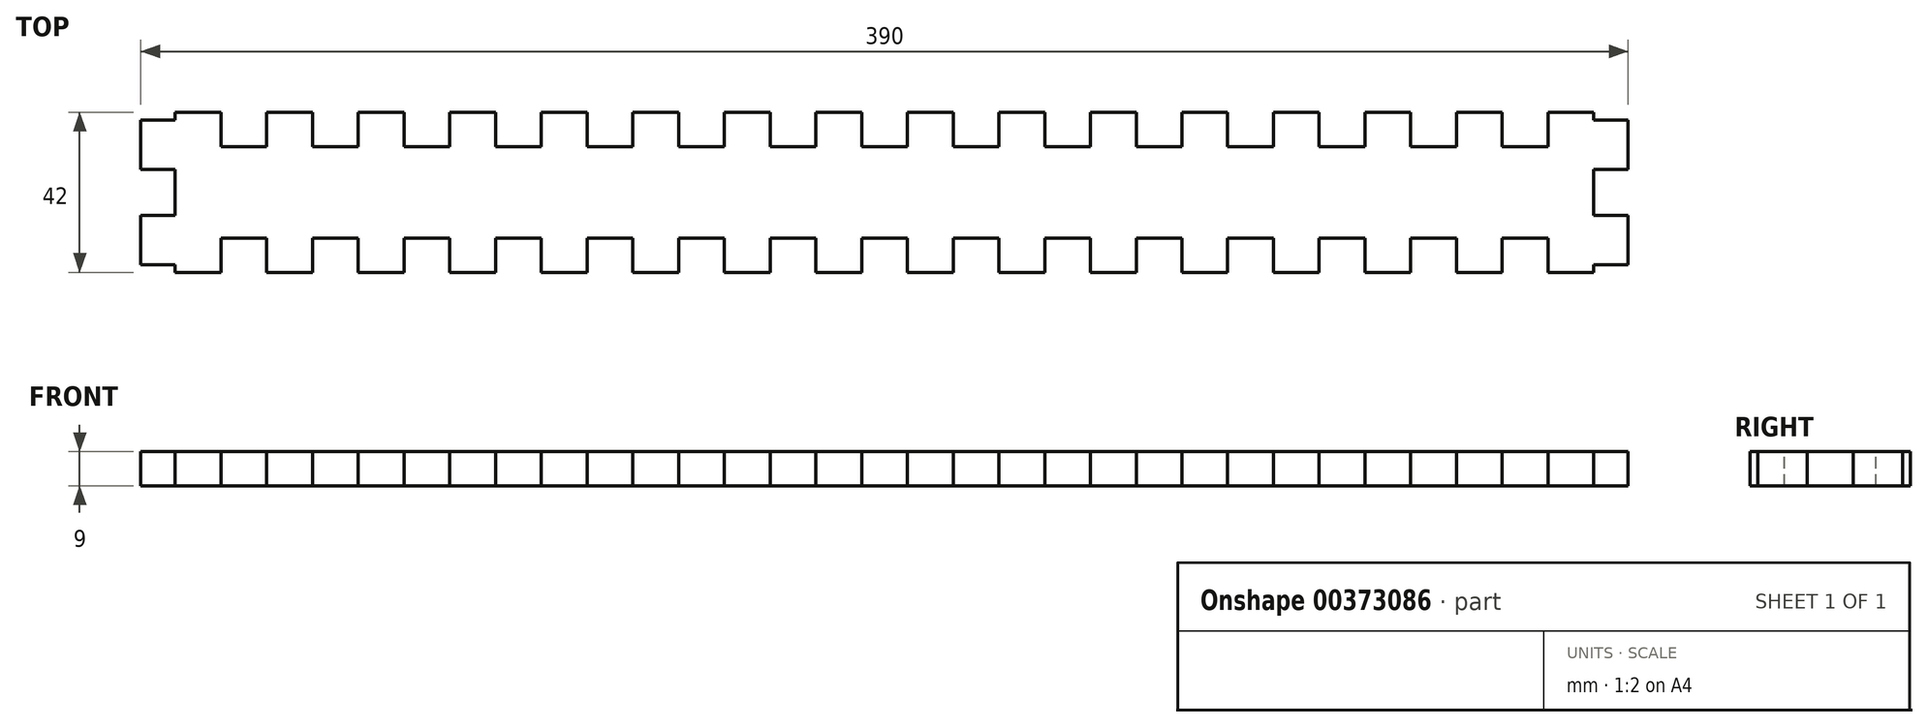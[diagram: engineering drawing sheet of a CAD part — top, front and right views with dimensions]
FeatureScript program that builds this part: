
annotation { "Feature Type Name" : "Feature", "Feature Type Description" : "" }
export const myFeature = defineFeature(function(context is Context, id is Id, definition is map)
    precondition{}
    {
        {
            var Q0;
            Q0=qCreatedBy(makeId("Top.planeOp"),FACE);
            var sketch = newSketch(context, id + "F0", { "sketchPlane" : qUnion([Q0])});
            skLineSegment(sketch, "E0.bottom", {"start": v(-198, 12) * mm, "end": v(198, 12) * mm});
            skLineSegment(sketch, "E0.top", {"start": v(-198, -12) * mm, "end": v(198, -12) * mm});
            skLineSegment(sketch, "E0.left", {"start": v(-198, 12) * mm, "end": v(-198, -12) * mm});
            skLineSegment(sketch, "E0.right", {"start": v(198, 12) * mm, "end": v(198, -12) * mm});
            skPoint(sketch, "E0.middle", {"position": v(0, 0) * mm});
            skSolve(sketch);
        }
        {
            var Q0;
            Q0 = qSketchRegion(id + "F0", true);
            extrude(context, id + "F1", {"entities" : qUnion([Q0]), "depth" : 9 * mm});
        }
        {
            var Q0;
            Q0=makeQuery(id+"F1.opExtrude","CAP_FACE",FACE,{"disambiguationData":[OSD([sQuery(id+"F0.wireOp",EDGE,"E0.bottom"),sQuery(id+"F0.wireOp",EDGE,"E0.top"),sQuery(id+"F0.wireOp",EDGE,"E0.left"),sQuery(id+"F0.wireOp",EDGE,"E0.right")])],"isStart":false});
            var sketch = newSketch(context, id + "F2", { "sketchPlane" : qUnion([Q0])});
            skLineSegment(sketch, "E1", {"start": v(0, 0) * mm, "end": v(0, -12) * mm, "construction": true});
            skLineSegment(sketch, "E2", {"start": v(0, -12) * mm, "end": v(6, -12) * mm, "construction": true});
            skLineSegment(sketch, "E3.bottom", {"start": v(6, -12) * mm, "end": v(18, -12) * mm});
            skLineSegment(sketch, "E3.top", {"start": v(6, -21) * mm, "end": v(18, -21) * mm});
            skLineSegment(sketch, "E3.left", {"start": v(6, -12) * mm, "end": v(6, -21) * mm});
            skLineSegment(sketch, "E3.right", {"start": v(18, -12) * mm, "end": v(18, -21) * mm});
            skLineSegment(sketch, "E4.direction1", {"start": v(6, -21) * mm, "end": v(18, -21) * mm, "construction": true});
            skLineSegment(sketch, "E5.1.0.0", {"start": v(30, -12) * mm, "end": v(30, -21) * mm});
            skLineSegment(sketch, "E5.1.0.1", {"start": v(30, -12) * mm, "end": v(42, -12) * mm});
            skLineSegment(sketch, "E5.1.0.2", {"start": v(42, -12) * mm, "end": v(42, -21) * mm});
            skLineSegment(sketch, "E5.1.0.3", {"start": v(30, -21) * mm, "end": v(42, -21) * mm});
            skLineSegment(sketch, "E5.2.0.0", {"start": v(54, -12) * mm, "end": v(54, -21) * mm});
            skLineSegment(sketch, "E5.2.0.1", {"start": v(54, -12) * mm, "end": v(66, -12) * mm});
            skLineSegment(sketch, "E5.2.0.2", {"start": v(66, -12) * mm, "end": v(66, -21) * mm});
            skLineSegment(sketch, "E5.2.0.3", {"start": v(54, -21) * mm, "end": v(66, -21) * mm});
            skLineSegment(sketch, "E5.3.0.0", {"start": v(78, -12) * mm, "end": v(78, -21) * mm});
            skLineSegment(sketch, "E5.3.0.1", {"start": v(78, -12) * mm, "end": v(90, -12) * mm});
            skLineSegment(sketch, "E5.3.0.2", {"start": v(90, -12) * mm, "end": v(90, -21) * mm});
            skLineSegment(sketch, "E5.3.0.3", {"start": v(78, -21) * mm, "end": v(90, -21) * mm});
            skLineSegment(sketch, "E5.4.0.0", {"start": v(102, -12) * mm, "end": v(102, -21) * mm});
            skLineSegment(sketch, "E5.4.0.1", {"start": v(102, -12) * mm, "end": v(114, -12) * mm});
            skLineSegment(sketch, "E5.4.0.2", {"start": v(114, -12) * mm, "end": v(114, -21) * mm});
            skLineSegment(sketch, "E5.4.0.3", {"start": v(102, -21) * mm, "end": v(114, -21) * mm});
            skLineSegment(sketch, "E5.5.0.0", {"start": v(126, -12) * mm, "end": v(126, -21) * mm});
            skLineSegment(sketch, "E5.5.0.1", {"start": v(126, -12) * mm, "end": v(138, -12) * mm});
            skLineSegment(sketch, "E5.5.0.2", {"start": v(138, -12) * mm, "end": v(138, -21) * mm});
            skLineSegment(sketch, "E5.5.0.3", {"start": v(126, -21) * mm, "end": v(138, -21) * mm});
            skLineSegment(sketch, "E5.6.0.0", {"start": v(150, -12) * mm, "end": v(150, -21) * mm});
            skLineSegment(sketch, "E5.6.0.1", {"start": v(150, -12) * mm, "end": v(162, -12) * mm});
            skLineSegment(sketch, "E5.6.0.2", {"start": v(162, -12) * mm, "end": v(162, -21) * mm});
            skLineSegment(sketch, "E5.6.0.3", {"start": v(150, -21) * mm, "end": v(162, -21) * mm});
            skLineSegment(sketch, "E5.7.0.0", {"start": v(174, -12) * mm, "end": v(174, -21) * mm});
            skLineSegment(sketch, "E5.7.0.1", {"start": v(174, -12) * mm, "end": v(186, -12) * mm});
            skLineSegment(sketch, "E5.7.0.2", {"start": v(186, -12) * mm, "end": v(186, -21) * mm});
            skLineSegment(sketch, "E5.7.0.3", {"start": v(174, -21) * mm, "end": v(186, -21) * mm});
            skLineSegment(sketch, "E5.direction1", {"start": v(6, -21) * mm, "end": v(30, -21) * mm, "construction": true});
            skLineSegment(sketch, "E6.MirrorCS", {"start": v(-6, -21) * mm, "end": v(-18, -21) * mm});
            skLineSegment(sketch, "E7.MirrorCS", {"start": v(0, -12) * mm, "end": v(-6, -12) * mm, "construction": true});
            skLineSegment(sketch, "E8.MirrorCS", {"start": v(-6, -12) * mm, "end": v(-6, -21) * mm});
            skLineSegment(sketch, "E9.MirrorCS", {"start": v(-6, -21) * mm, "end": v(-18, -21) * mm, "construction": true});
            skLineSegment(sketch, "E10.MirrorCS", {"start": v(-6, -21) * mm, "end": v(-30, -21) * mm, "construction": true});
            skLineSegment(sketch, "E11.MirrorCS", {"start": v(-66, -12) * mm, "end": v(-66, -21) * mm});
            skLineSegment(sketch, "E12.MirrorCS", {"start": v(-54, -21) * mm, "end": v(-66, -21) * mm});
            skLineSegment(sketch, "E13.MirrorCS", {"start": v(-78, -12) * mm, "end": v(-78, -21) * mm});
            skLineSegment(sketch, "E14.MirrorCS", {"start": v(-6, -12) * mm, "end": v(-18, -12) * mm});
            skLineSegment(sketch, "E15.MirrorCS", {"start": v(-126, -12) * mm, "end": v(-126, -21) * mm});
            skLineSegment(sketch, "E16.MirrorCS", {"start": v(-150, -12) * mm, "end": v(-150, -21) * mm});
            skLineSegment(sketch, "E17.MirrorCS", {"start": v(-162, -12) * mm, "end": v(-162, -21) * mm});
            skLineSegment(sketch, "E18.MirrorCS", {"start": v(-18, -12) * mm, "end": v(-18, -21) * mm});
            skLineSegment(sketch, "E19.MirrorCS", {"start": v(-30, -12) * mm, "end": v(-30, -21) * mm});
            skLineSegment(sketch, "E20.MirrorCS", {"start": v(-30, -12) * mm, "end": v(-42, -12) * mm});
            skLineSegment(sketch, "E21.MirrorCS", {"start": v(-102, -12) * mm, "end": v(-114, -12) * mm});
            skLineSegment(sketch, "E22.MirrorCS", {"start": v(-174, -12) * mm, "end": v(-186, -12) * mm});
            skLineSegment(sketch, "E23.MirrorCS", {"start": v(-42, -12) * mm, "end": v(-42, -21) * mm});
            skLineSegment(sketch, "E24.MirrorCS", {"start": v(-30, -21) * mm, "end": v(-42, -21) * mm});
            skLineSegment(sketch, "E25.MirrorCS", {"start": v(-54, -12) * mm, "end": v(-54, -21) * mm});
            skLineSegment(sketch, "E26.MirrorCS", {"start": v(-138, -12) * mm, "end": v(-138, -21) * mm});
            skLineSegment(sketch, "E27.MirrorCS", {"start": v(-54, -12) * mm, "end": v(-66, -12) * mm});
            skLineSegment(sketch, "E28.MirrorCS", {"start": v(-78, -12) * mm, "end": v(-90, -12) * mm});
            skLineSegment(sketch, "E29.MirrorCS", {"start": v(-174, -12) * mm, "end": v(-174, -21) * mm});
            skLineSegment(sketch, "E30.MirrorCS", {"start": v(-102, -21) * mm, "end": v(-114, -21) * mm});
            skLineSegment(sketch, "E31.MirrorCS", {"start": v(-174, -21) * mm, "end": v(-186, -21) * mm});
            skLineSegment(sketch, "E32.MirrorCS", {"start": v(-78, -21) * mm, "end": v(-90, -21) * mm});
            skLineSegment(sketch, "E33.MirrorCS", {"start": v(-150, -12) * mm, "end": v(-162, -12) * mm});
            skLineSegment(sketch, "E34.MirrorCS", {"start": v(-126, -21) * mm, "end": v(-138, -21) * mm});
            skLineSegment(sketch, "E35.MirrorCS", {"start": v(-150, -21) * mm, "end": v(-162, -21) * mm});
            skLineSegment(sketch, "E36.MirrorCS", {"start": v(-114, -12) * mm, "end": v(-114, -21) * mm});
            skLineSegment(sketch, "E37.MirrorCS", {"start": v(-102, -12) * mm, "end": v(-102, -21) * mm});
            skLineSegment(sketch, "E38.MirrorCS", {"start": v(-90, -12) * mm, "end": v(-90, -21) * mm});
            skLineSegment(sketch, "E39.MirrorCS", {"start": v(-126, -12) * mm, "end": v(-138, -12) * mm});
            skLineSegment(sketch, "E40.MirrorCS", {"start": v(-186, -12) * mm, "end": v(-186, -21) * mm});
            skLineSegment(sketch, "E41", {"start": v(-198, 0) * mm, "end": v(-171.64, 0) * mm, "construction": true});
            skPoint(sketch, "E41.endSnap0", {"position": v(-198, 0) * mm});
            skLineSegment(sketch, "E42.MirrorCS", {"start": v(6, 12) * mm, "end": v(6, 21) * mm});
            skLineSegment(sketch, "E43.MirrorCS", {"start": v(-6, 21) * mm, "end": v(-18, 21) * mm});
            skLineSegment(sketch, "E44.MirrorCS", {"start": v(0, 12) * mm, "end": v(6, 12) * mm, "construction": true});
            skLineSegment(sketch, "E45.MirrorCS", {"start": v(6, 21) * mm, "end": v(18, 21) * mm});
            skLineSegment(sketch, "E46.MirrorCS", {"start": v(0, 12) * mm, "end": v(-6, 12) * mm, "construction": true});
            skLineSegment(sketch, "E47.MirrorCS", {"start": v(-6, 12) * mm, "end": v(-6, 21) * mm});
            skLineSegment(sketch, "E48.MirrorCS", {"start": v(-6, 12) * mm, "end": v(-18, 12) * mm});
            skLineSegment(sketch, "E49.MirrorCS", {"start": v(30, 12) * mm, "end": v(42, 12) * mm});
            skLineSegment(sketch, "E50.MirrorCS", {"start": v(6, 12) * mm, "end": v(18, 12) * mm});
            skLineSegment(sketch, "E51.MirrorCS", {"start": v(-6, 21) * mm, "end": v(-30, 21) * mm, "construction": true});
            skLineSegment(sketch, "E52.MirrorCS", {"start": v(6, 21) * mm, "end": v(18, 21) * mm, "construction": true});
            skLineSegment(sketch, "E53.MirrorCS", {"start": v(6, 21) * mm, "end": v(30, 21) * mm, "construction": true});
            skLineSegment(sketch, "E54.MirrorCS", {"start": v(30, 12) * mm, "end": v(30, 21) * mm});
            skLineSegment(sketch, "E55.MirrorCS", {"start": v(-30, 12) * mm, "end": v(-30, 21) * mm});
            skLineSegment(sketch, "E56.MirrorCS", {"start": v(-6, 21) * mm, "end": v(-18, 21) * mm, "construction": true});
            skLineSegment(sketch, "E57.MirrorCS", {"start": v(-78, 12) * mm, "end": v(-78, 21) * mm});
            skLineSegment(sketch, "E58.MirrorCS", {"start": v(150, 12) * mm, "end": v(162, 12) * mm});
            skLineSegment(sketch, "E59.MirrorCS", {"start": v(-54, 21) * mm, "end": v(-66, 21) * mm});
            skLineSegment(sketch, "E60.MirrorCS", {"start": v(78, 12) * mm, "end": v(78, 21) * mm});
            skLineSegment(sketch, "E61.MirrorCS", {"start": v(-54, 12) * mm, "end": v(-54, 21) * mm});
            skLineSegment(sketch, "E62.MirrorCS", {"start": v(-30, 21) * mm, "end": v(-42, 21) * mm});
            skLineSegment(sketch, "E63.MirrorCS", {"start": v(102, 21) * mm, "end": v(114, 21) * mm});
            skLineSegment(sketch, "E64.MirrorCS", {"start": v(-150, 12) * mm, "end": v(-162, 12) * mm});
            skLineSegment(sketch, "E65.MirrorCS", {"start": v(-186, 12) * mm, "end": v(-186, 21) * mm});
            skLineSegment(sketch, "E66.MirrorCS", {"start": v(-174, 21) * mm, "end": v(-186, 21) * mm});
            skLineSegment(sketch, "E67.MirrorCS", {"start": v(-102, 12) * mm, "end": v(-114, 12) * mm});
            skLineSegment(sketch, "E68.MirrorCS", {"start": v(-78, 12) * mm, "end": v(-90, 12) * mm});
            skLineSegment(sketch, "E69.MirrorCS", {"start": v(-66, 12) * mm, "end": v(-66, 21) * mm});
            skLineSegment(sketch, "E70.MirrorCS", {"start": v(-54, 12) * mm, "end": v(-66, 12) * mm});
            skLineSegment(sketch, "E71.MirrorCS", {"start": v(174, 21) * mm, "end": v(186, 21) * mm});
            skLineSegment(sketch, "E72.MirrorCS", {"start": v(30, 21) * mm, "end": v(42, 21) * mm});
            skLineSegment(sketch, "E73.MirrorCS", {"start": v(150, 21) * mm, "end": v(162, 21) * mm});
            skLineSegment(sketch, "E74.MirrorCS", {"start": v(-102, 21) * mm, "end": v(-114, 21) * mm});
            skLineSegment(sketch, "E75.MirrorCS", {"start": v(-102, 12) * mm, "end": v(-102, 21) * mm});
            skLineSegment(sketch, "E76.MirrorCS", {"start": v(126, 21) * mm, "end": v(138, 21) * mm});
            skLineSegment(sketch, "E77.MirrorCS", {"start": v(-114, 12) * mm, "end": v(-114, 21) * mm});
            skLineSegment(sketch, "E78.MirrorCS", {"start": v(102, 12) * mm, "end": v(114, 12) * mm});
            skLineSegment(sketch, "E79.MirrorCS", {"start": v(114, 12) * mm, "end": v(114, 21) * mm});
            skLineSegment(sketch, "E80.MirrorCS", {"start": v(-30, 12) * mm, "end": v(-42, 12) * mm});
            skLineSegment(sketch, "E81.MirrorCS", {"start": v(78, 21) * mm, "end": v(90, 21) * mm});
            skLineSegment(sketch, "E82.MirrorCS", {"start": v(54, 12) * mm, "end": v(66, 12) * mm});
            skLineSegment(sketch, "E83.MirrorCS", {"start": v(18, 12) * mm, "end": v(18, 21) * mm});
            skLineSegment(sketch, "E84.MirrorCS", {"start": v(54, 21) * mm, "end": v(66, 21) * mm});
            skLineSegment(sketch, "E85.MirrorCS", {"start": v(-150, 21) * mm, "end": v(-162, 21) * mm});
            skLineSegment(sketch, "E86.MirrorCS", {"start": v(-150, 12) * mm, "end": v(-150, 21) * mm});
            skLineSegment(sketch, "E87.MirrorCS", {"start": v(78, 12) * mm, "end": v(90, 12) * mm});
            skLineSegment(sketch, "E88.MirrorCS", {"start": v(174, 12) * mm, "end": v(186, 12) * mm});
            skLineSegment(sketch, "E89.MirrorCS", {"start": v(-174, 12) * mm, "end": v(-186, 12) * mm});
            skLineSegment(sketch, "E90.MirrorCS", {"start": v(102, 12) * mm, "end": v(102, 21) * mm});
            skLineSegment(sketch, "E91.MirrorCS", {"start": v(150, 12) * mm, "end": v(150, 21) * mm});
            skLineSegment(sketch, "E92.MirrorCS", {"start": v(162, 12) * mm, "end": v(162, 21) * mm});
            skLineSegment(sketch, "E93.MirrorCS", {"start": v(-174, 12) * mm, "end": v(-174, 21) * mm});
            skLineSegment(sketch, "E94.MirrorCS", {"start": v(138, 12) * mm, "end": v(138, 21) * mm});
            skLineSegment(sketch, "E95.MirrorCS", {"start": v(54, 12) * mm, "end": v(54, 21) * mm});
            skLineSegment(sketch, "E96.MirrorCS", {"start": v(42, 12) * mm, "end": v(42, 21) * mm});
            skLineSegment(sketch, "E97.MirrorCS", {"start": v(66, 12) * mm, "end": v(66, 21) * mm});
            skLineSegment(sketch, "E98.MirrorCS", {"start": v(186, 12) * mm, "end": v(186, 21) * mm});
            skLineSegment(sketch, "E99.MirrorCS", {"start": v(126, 12) * mm, "end": v(138, 12) * mm});
            skLineSegment(sketch, "E100.MirrorCS", {"start": v(-138, 12) * mm, "end": v(-138, 21) * mm});
            skLineSegment(sketch, "E101.MirrorCS", {"start": v(90, 12) * mm, "end": v(90, 21) * mm});
            skLineSegment(sketch, "E102.MirrorCS", {"start": v(-126, 21) * mm, "end": v(-138, 21) * mm});
            skLineSegment(sketch, "E103.MirrorCS", {"start": v(-162, 12) * mm, "end": v(-162, 21) * mm});
            skLineSegment(sketch, "E104.MirrorCS", {"start": v(126, 12) * mm, "end": v(126, 21) * mm});
            skLineSegment(sketch, "E105.MirrorCS", {"start": v(-18, 12) * mm, "end": v(-18, 21) * mm});
            skLineSegment(sketch, "E106.MirrorCS", {"start": v(-42, 12) * mm, "end": v(-42, 21) * mm});
            skLineSegment(sketch, "E107.MirrorCS", {"start": v(-78, 21) * mm, "end": v(-90, 21) * mm});
            skLineSegment(sketch, "E108.MirrorCS", {"start": v(-90, 12) * mm, "end": v(-90, 21) * mm});
            skLineSegment(sketch, "E109.MirrorCS", {"start": v(-126, 12) * mm, "end": v(-126, 21) * mm});
            skLineSegment(sketch, "E110.MirrorCS", {"start": v(-126, 12) * mm, "end": v(-138, 12) * mm});
            skLineSegment(sketch, "E111.MirrorCS", {"start": v(174, 12) * mm, "end": v(174, 21) * mm});
            skSolve(sketch);
        }
        {
            var Q0;
            Q0 = qSketchRegion(id + "F2", true);
            var Q1;
            Q1=makeQuery(id+"F1.opExtrude","CAP_FACE",FACE,{"disambiguationData":[OSD([sQuery(id+"F0.wireOp",EDGE,"E0.bottom"),sQuery(id+"F0.wireOp",EDGE,"E0.top"),sQuery(id+"F0.wireOp",EDGE,"E0.left"),sQuery(id+"F0.wireOp",EDGE,"E0.right")])],"isStart":true});
            extrude(context, id + "F3", {"entities" : qUnion([Q0]), "operationType" : NewBodyOperationType.ADD, "endBound" : BoundingType.UP_TO_SURFACE, "oppositeDirection" : true, "endBoundEntityFace" : qUnion([Q1]), "depth" : 25 * mm});
        }
        {
            var Q0;
            {var subQ0=sQuery(id+"F0.wireOp",EDGE,"E0.right");var subQ1=sQuery(id+"F0.wireOp",EDGE,"E0.left");var subQ2=sQuery(id+"F0.wireOp",EDGE,"E0.top");var subQ3=sQuery(id+"F0.wireOp",EDGE,"E0.bottom");Q0=makeQuery(id+"F3.boolean.opBoolean","MERGE",FACE,{"derivedFrom":[makeQuery(id+"F1.opExtrude","CAP_FACE",FACE,{"disambiguationData":[OSD([subQ3,subQ2,subQ1,subQ0])],"isStart":true}),makeQuery(id+"F3.opExtrude","CAP_FACE",FACE,{"disambiguationData":[OSD([subQ3,subQ2,subQ1,subQ0]),ownerDisambiguation([makeQuery(id+"F2.imprint","IMPRINT",EDGE,{"derivedFrom":sQuery(id+"F2.wireOp",EDGE,"E3.bottom")})])],"isStart":false}),makeQuery(id+"F3.opExtrude","CAP_FACE",FACE,{"disambiguationData":[OSD([subQ3,subQ2,subQ1,subQ0]),ownerDisambiguation([makeQuery(id+"F2.imprint","IMPRINT",EDGE,{"derivedFrom":sQuery(id+"F2.wireOp",EDGE,"E5.1.0.0")})])],"isStart":false}),makeQuery(id+"F3.opExtrude","CAP_FACE",FACE,{"disambiguationData":[OSD([subQ3,subQ2,subQ1,subQ0]),ownerDisambiguation([makeQuery(id+"F2.imprint","IMPRINT",EDGE,{"derivedFrom":sQuery(id+"F2.wireOp",EDGE,"E5.2.0.0")})])],"isStart":false}),makeQuery(id+"F3.opExtrude","CAP_FACE",FACE,{"disambiguationData":[OSD([subQ3,subQ2,subQ1,subQ0]),ownerDisambiguation([makeQuery(id+"F2.imprint","IMPRINT",EDGE,{"derivedFrom":sQuery(id+"F2.wireOp",EDGE,"E5.3.0.0")})])],"isStart":false}),makeQuery(id+"F3.opExtrude","CAP_FACE",FACE,{"disambiguationData":[OSD([subQ3,subQ2,subQ1,subQ0]),ownerDisambiguation([makeQuery(id+"F2.imprint","IMPRINT",EDGE,{"derivedFrom":sQuery(id+"F2.wireOp",EDGE,"E5.4.0.0")})])],"isStart":false}),makeQuery(id+"F3.opExtrude","CAP_FACE",FACE,{"disambiguationData":[OSD([subQ3,subQ2,subQ1,subQ0]),ownerDisambiguation([makeQuery(id+"F2.imprint","IMPRINT",EDGE,{"derivedFrom":sQuery(id+"F2.wireOp",EDGE,"E5.5.0.0")})])],"isStart":false}),makeQuery(id+"F3.opExtrude","CAP_FACE",FACE,{"disambiguationData":[OSD([subQ3,subQ2,subQ1,subQ0]),ownerDisambiguation([makeQuery(id+"F2.imprint","IMPRINT",EDGE,{"derivedFrom":sQuery(id+"F2.wireOp",EDGE,"E5.6.0.0")})])],"isStart":false}),makeQuery(id+"F3.opExtrude","CAP_FACE",FACE,{"disambiguationData":[OSD([subQ3,subQ2,subQ1,subQ0]),ownerDisambiguation([makeQuery(id+"F2.imprint","IMPRINT",EDGE,{"derivedFrom":sQuery(id+"F2.wireOp",EDGE,"E5.7.0.0")})])],"isStart":false}),makeQuery(id+"F3.opExtrude","CAP_FACE",FACE,{"disambiguationData":[OSD([subQ3,subQ2,subQ1,subQ0]),ownerDisambiguation([makeQuery(id+"F2.imprint","IMPRINT",EDGE,{"derivedFrom":sQuery(id+"F2.wireOp",EDGE,"E6.MirrorCS")})])],"isStart":false}),makeQuery(id+"F3.opExtrude","CAP_FACE",FACE,{"disambiguationData":[OSD([subQ3,subQ2,subQ1,subQ0]),ownerDisambiguation([makeQuery(id+"F2.imprint","IMPRINT",EDGE,{"derivedFrom":sQuery(id+"F2.wireOp",EDGE,"E11.MirrorCS")})])],"isStart":false}),makeQuery(id+"F3.opExtrude","CAP_FACE",FACE,{"disambiguationData":[OSD([subQ3,subQ2,subQ1,subQ0]),ownerDisambiguation([makeQuery(id+"F2.imprint","IMPRINT",EDGE,{"derivedFrom":sQuery(id+"F2.wireOp",EDGE,"E13.MirrorCS")})])],"isStart":false}),makeQuery(id+"F3.opExtrude","CAP_FACE",FACE,{"disambiguationData":[OSD([subQ3,subQ2,subQ1,subQ0]),ownerDisambiguation([makeQuery(id+"F2.imprint","IMPRINT",EDGE,{"derivedFrom":sQuery(id+"F2.wireOp",EDGE,"E15.MirrorCS")})])],"isStart":false}),makeQuery(id+"F3.opExtrude","CAP_FACE",FACE,{"disambiguationData":[OSD([subQ3,subQ2,subQ1,subQ0]),ownerDisambiguation([makeQuery(id+"F2.imprint","IMPRINT",EDGE,{"derivedFrom":sQuery(id+"F2.wireOp",EDGE,"E16.MirrorCS")})])],"isStart":false}),makeQuery(id+"F3.opExtrude","CAP_FACE",FACE,{"disambiguationData":[OSD([subQ3,subQ2,subQ1,subQ0]),ownerDisambiguation([makeQuery(id+"F2.imprint","IMPRINT",EDGE,{"derivedFrom":sQuery(id+"F2.wireOp",EDGE,"E19.MirrorCS")})])],"isStart":false}),makeQuery(id+"F3.opExtrude","CAP_FACE",FACE,{"disambiguationData":[OSD([subQ3,subQ2,subQ1,subQ0]),ownerDisambiguation([makeQuery(id+"F2.imprint","IMPRINT",EDGE,{"derivedFrom":sQuery(id+"F2.wireOp",EDGE,"E21.MirrorCS")})])],"isStart":false}),makeQuery(id+"F3.opExtrude","CAP_FACE",FACE,{"disambiguationData":[OSD([subQ3,subQ2,subQ1,subQ0]),ownerDisambiguation([makeQuery(id+"F2.imprint","IMPRINT",EDGE,{"derivedFrom":sQuery(id+"F2.wireOp",EDGE,"E22.MirrorCS")})])],"isStart":false}),makeQuery(id+"F3.opExtrude","CAP_FACE",FACE,{"disambiguationData":[OSD([subQ3,subQ2,subQ1,subQ0]),ownerDisambiguation([makeQuery(id+"F2.imprint","IMPRINT",EDGE,{"derivedFrom":sQuery(id+"F2.wireOp",EDGE,"E42.MirrorCS")})])],"isStart":false}),makeQuery(id+"F3.opExtrude","CAP_FACE",FACE,{"disambiguationData":[OSD([subQ3,subQ2,subQ1,subQ0]),ownerDisambiguation([makeQuery(id+"F2.imprint","IMPRINT",EDGE,{"derivedFrom":sQuery(id+"F2.wireOp",EDGE,"E43.MirrorCS")})])],"isStart":false}),makeQuery(id+"F3.opExtrude","CAP_FACE",FACE,{"disambiguationData":[OSD([subQ3,subQ2,subQ1,subQ0]),ownerDisambiguation([makeQuery(id+"F2.imprint","IMPRINT",EDGE,{"derivedFrom":sQuery(id+"F2.wireOp",EDGE,"E49.MirrorCS")})])],"isStart":false}),makeQuery(id+"F3.opExtrude","CAP_FACE",FACE,{"disambiguationData":[OSD([subQ3,subQ2,subQ1,subQ0]),ownerDisambiguation([makeQuery(id+"F2.imprint","IMPRINT",EDGE,{"derivedFrom":sQuery(id+"F2.wireOp",EDGE,"E55.MirrorCS")})])],"isStart":false}),makeQuery(id+"F3.opExtrude","CAP_FACE",FACE,{"disambiguationData":[OSD([subQ3,subQ2,subQ1,subQ0]),ownerDisambiguation([makeQuery(id+"F2.imprint","IMPRINT",EDGE,{"derivedFrom":sQuery(id+"F2.wireOp",EDGE,"E57.MirrorCS")})])],"isStart":false}),makeQuery(id+"F3.opExtrude","CAP_FACE",FACE,{"disambiguationData":[OSD([subQ3,subQ2,subQ1,subQ0]),ownerDisambiguation([makeQuery(id+"F2.imprint","IMPRINT",EDGE,{"derivedFrom":sQuery(id+"F2.wireOp",EDGE,"E58.MirrorCS")})])],"isStart":false}),makeQuery(id+"F3.opExtrude","CAP_FACE",FACE,{"disambiguationData":[OSD([subQ3,subQ2,subQ1,subQ0]),ownerDisambiguation([makeQuery(id+"F2.imprint","IMPRINT",EDGE,{"derivedFrom":sQuery(id+"F2.wireOp",EDGE,"E59.MirrorCS")})])],"isStart":false}),makeQuery(id+"F3.opExtrude","CAP_FACE",FACE,{"disambiguationData":[OSD([subQ3,subQ2,subQ1,subQ0]),ownerDisambiguation([makeQuery(id+"F2.imprint","IMPRINT",EDGE,{"derivedFrom":sQuery(id+"F2.wireOp",EDGE,"E60.MirrorCS")})])],"isStart":false}),makeQuery(id+"F3.opExtrude","CAP_FACE",FACE,{"disambiguationData":[OSD([subQ3,subQ2,subQ1,subQ0]),ownerDisambiguation([makeQuery(id+"F2.imprint","IMPRINT",EDGE,{"derivedFrom":sQuery(id+"F2.wireOp",EDGE,"E63.MirrorCS")})])],"isStart":false}),makeQuery(id+"F3.opExtrude","CAP_FACE",FACE,{"disambiguationData":[OSD([subQ3,subQ2,subQ1,subQ0]),ownerDisambiguation([makeQuery(id+"F2.imprint","IMPRINT",EDGE,{"derivedFrom":sQuery(id+"F2.wireOp",EDGE,"E64.MirrorCS")})])],"isStart":false}),makeQuery(id+"F3.opExtrude","CAP_FACE",FACE,{"disambiguationData":[OSD([subQ3,subQ2,subQ1,subQ0]),ownerDisambiguation([makeQuery(id+"F2.imprint","IMPRINT",EDGE,{"derivedFrom":sQuery(id+"F2.wireOp",EDGE,"E65.MirrorCS")})])],"isStart":false}),makeQuery(id+"F3.opExtrude","CAP_FACE",FACE,{"disambiguationData":[OSD([subQ3,subQ2,subQ1,subQ0]),ownerDisambiguation([makeQuery(id+"F2.imprint","IMPRINT",EDGE,{"derivedFrom":sQuery(id+"F2.wireOp",EDGE,"E67.MirrorCS")})])],"isStart":false}),makeQuery(id+"F3.opExtrude","CAP_FACE",FACE,{"disambiguationData":[OSD([subQ3,subQ2,subQ1,subQ0]),ownerDisambiguation([makeQuery(id+"F2.imprint","IMPRINT",EDGE,{"derivedFrom":sQuery(id+"F2.wireOp",EDGE,"E71.MirrorCS")})])],"isStart":false}),makeQuery(id+"F3.opExtrude","CAP_FACE",FACE,{"disambiguationData":[OSD([subQ3,subQ2,subQ1,subQ0]),ownerDisambiguation([makeQuery(id+"F2.imprint","IMPRINT",EDGE,{"derivedFrom":sQuery(id+"F2.wireOp",EDGE,"E76.MirrorCS")})])],"isStart":false}),makeQuery(id+"F3.opExtrude","CAP_FACE",FACE,{"disambiguationData":[OSD([subQ3,subQ2,subQ1,subQ0]),ownerDisambiguation([makeQuery(id+"F2.imprint","IMPRINT",EDGE,{"derivedFrom":sQuery(id+"F2.wireOp",EDGE,"E82.MirrorCS")})])],"isStart":false}),makeQuery(id+"F3.opExtrude","CAP_FACE",FACE,{"disambiguationData":[OSD([subQ3,subQ2,subQ1,subQ0]),ownerDisambiguation([makeQuery(id+"F2.imprint","IMPRINT",EDGE,{"derivedFrom":sQuery(id+"F2.wireOp",EDGE,"E100.MirrorCS")})])],"isStart":false})]});}
            var sketch = newSketch(context, id + "F4", { "sketchPlane" : qUnion([Q0])});
            skLineSegment(sketch, "E112", {"start": v(-198, 0) * mm, "end": v(-189, 0) * mm, "construction": true});
            skPoint(sketch, "E112.endSnap0", {"position": v(-198, 0) * mm});
            skLineSegment(sketch, "E113.bottom", {"start": v(-198, 6) * mm, "end": v(-189, 6) * mm});
            skLineSegment(sketch, "E113.top", {"start": v(-198, -6) * mm, "end": v(-189, -6) * mm});
            skLineSegment(sketch, "E113.left", {"start": v(-198, 6) * mm, "end": v(-198, -6) * mm});
            skLineSegment(sketch, "E113.right", {"start": v(-189, 6) * mm, "end": v(-189, -6) * mm});
            skPoint(sketch, "E113.middle", {"position": v(-193.5, 0) * mm});
            skLineSegment(sketch, "E114", {"start": v(0, 0) * mm, "end": v(0, 7.64) * mm, "construction": true});
            skLineSegment(sketch, "E115.MirrorCS", {"start": v(198, 6) * mm, "end": v(198, -6) * mm});
            skLineSegment(sketch, "E116.MirrorCS", {"start": v(198, -6) * mm, "end": v(189, -6) * mm});
            skLineSegment(sketch, "E117.MirrorCS", {"start": v(198, 0) * mm, "end": v(189, 0) * mm, "construction": true});
            skPoint(sketch, "E118.MirrorP", {"position": v(198, 0) * mm});
            skLineSegment(sketch, "E119.MirrorCS", {"start": v(189, 6) * mm, "end": v(189, -6) * mm});
            skLineSegment(sketch, "E120.MirrorCS", {"start": v(198, 6) * mm, "end": v(189, 6) * mm});
            skPoint(sketch, "E121.MirrorP", {"position": v(193.5, 0) * mm});
            skSolve(sketch);
        }
        {
            var Q0;
            Q0=makeQuery(id+"F4.imprint","IMPRINT",FACE,{"disambiguationData":[TD([[makeQuery(id+"F4.imprint","IMPRINT",EDGE,{"derivedFrom":sQuery(id+"F4.wireOp",EDGE,"E113.bottom")}),-1.0]])]});
            var Q1;
            Q1=makeQuery(id+"F4.imprint","IMPRINT",FACE,{"disambiguationData":[TD([[makeQuery(id+"F4.imprint","IMPRINT",EDGE,{"derivedFrom":sQuery(id+"F4.wireOp",EDGE,"E115.MirrorCS")}),1.0]])]});
            extrude(context, id + "F5", {"entities" : qUnion([Q0, Q1]), "operationType" : NewBodyOperationType.REMOVE, "endBound" : BoundingType.THROUGH_ALL, "oppositeDirection" : true, "depth" : 25 * mm});
        }
        {
            var Q0;
            {var subQ0=sQuery(id+"F0.wireOp",EDGE,"E0.right");var subQ1=sQuery(id+"F0.wireOp",EDGE,"E0.left");var subQ2=sQuery(id+"F0.wireOp",EDGE,"E0.top");var subQ3=sQuery(id+"F0.wireOp",EDGE,"E0.bottom");Q0=makeQuery(id+"F3.boolean.opBoolean","MERGE",FACE,{"derivedFrom":[makeQuery(id+"F1.opExtrude","CAP_FACE",FACE,{"disambiguationData":[OSD([subQ3,subQ2,subQ1,subQ0])],"isStart":true}),makeQuery(id+"F3.opExtrude","CAP_FACE",FACE,{"disambiguationData":[OSD([subQ3,subQ2,subQ1,subQ0]),ownerDisambiguation([makeQuery(id+"F2.imprint","IMPRINT",EDGE,{"derivedFrom":sQuery(id+"F2.wireOp",EDGE,"E3.bottom")})])],"isStart":false}),makeQuery(id+"F3.opExtrude","CAP_FACE",FACE,{"disambiguationData":[OSD([subQ3,subQ2,subQ1,subQ0]),ownerDisambiguation([makeQuery(id+"F2.imprint","IMPRINT",EDGE,{"derivedFrom":sQuery(id+"F2.wireOp",EDGE,"E5.1.0.0")})])],"isStart":false}),makeQuery(id+"F3.opExtrude","CAP_FACE",FACE,{"disambiguationData":[OSD([subQ3,subQ2,subQ1,subQ0]),ownerDisambiguation([makeQuery(id+"F2.imprint","IMPRINT",EDGE,{"derivedFrom":sQuery(id+"F2.wireOp",EDGE,"E5.2.0.0")})])],"isStart":false}),makeQuery(id+"F3.opExtrude","CAP_FACE",FACE,{"disambiguationData":[OSD([subQ3,subQ2,subQ1,subQ0]),ownerDisambiguation([makeQuery(id+"F2.imprint","IMPRINT",EDGE,{"derivedFrom":sQuery(id+"F2.wireOp",EDGE,"E5.3.0.0")})])],"isStart":false}),makeQuery(id+"F3.opExtrude","CAP_FACE",FACE,{"disambiguationData":[OSD([subQ3,subQ2,subQ1,subQ0]),ownerDisambiguation([makeQuery(id+"F2.imprint","IMPRINT",EDGE,{"derivedFrom":sQuery(id+"F2.wireOp",EDGE,"E5.4.0.0")})])],"isStart":false}),makeQuery(id+"F3.opExtrude","CAP_FACE",FACE,{"disambiguationData":[OSD([subQ3,subQ2,subQ1,subQ0]),ownerDisambiguation([makeQuery(id+"F2.imprint","IMPRINT",EDGE,{"derivedFrom":sQuery(id+"F2.wireOp",EDGE,"E5.5.0.0")})])],"isStart":false}),makeQuery(id+"F3.opExtrude","CAP_FACE",FACE,{"disambiguationData":[OSD([subQ3,subQ2,subQ1,subQ0]),ownerDisambiguation([makeQuery(id+"F2.imprint","IMPRINT",EDGE,{"derivedFrom":sQuery(id+"F2.wireOp",EDGE,"E5.6.0.0")})])],"isStart":false}),makeQuery(id+"F3.opExtrude","CAP_FACE",FACE,{"disambiguationData":[OSD([subQ3,subQ2,subQ1,subQ0]),ownerDisambiguation([makeQuery(id+"F2.imprint","IMPRINT",EDGE,{"derivedFrom":sQuery(id+"F2.wireOp",EDGE,"E5.7.0.0")})])],"isStart":false}),makeQuery(id+"F3.opExtrude","CAP_FACE",FACE,{"disambiguationData":[OSD([subQ3,subQ2,subQ1,subQ0]),ownerDisambiguation([makeQuery(id+"F2.imprint","IMPRINT",EDGE,{"derivedFrom":sQuery(id+"F2.wireOp",EDGE,"E6.MirrorCS")})])],"isStart":false}),makeQuery(id+"F3.opExtrude","CAP_FACE",FACE,{"disambiguationData":[OSD([subQ3,subQ2,subQ1,subQ0]),ownerDisambiguation([makeQuery(id+"F2.imprint","IMPRINT",EDGE,{"derivedFrom":sQuery(id+"F2.wireOp",EDGE,"E11.MirrorCS")})])],"isStart":false}),makeQuery(id+"F3.opExtrude","CAP_FACE",FACE,{"disambiguationData":[OSD([subQ3,subQ2,subQ1,subQ0]),ownerDisambiguation([makeQuery(id+"F2.imprint","IMPRINT",EDGE,{"derivedFrom":sQuery(id+"F2.wireOp",EDGE,"E13.MirrorCS")})])],"isStart":false}),makeQuery(id+"F3.opExtrude","CAP_FACE",FACE,{"disambiguationData":[OSD([subQ3,subQ2,subQ1,subQ0]),ownerDisambiguation([makeQuery(id+"F2.imprint","IMPRINT",EDGE,{"derivedFrom":sQuery(id+"F2.wireOp",EDGE,"E15.MirrorCS")})])],"isStart":false}),makeQuery(id+"F3.opExtrude","CAP_FACE",FACE,{"disambiguationData":[OSD([subQ3,subQ2,subQ1,subQ0]),ownerDisambiguation([makeQuery(id+"F2.imprint","IMPRINT",EDGE,{"derivedFrom":sQuery(id+"F2.wireOp",EDGE,"E16.MirrorCS")})])],"isStart":false}),makeQuery(id+"F3.opExtrude","CAP_FACE",FACE,{"disambiguationData":[OSD([subQ3,subQ2,subQ1,subQ0]),ownerDisambiguation([makeQuery(id+"F2.imprint","IMPRINT",EDGE,{"derivedFrom":sQuery(id+"F2.wireOp",EDGE,"E19.MirrorCS")})])],"isStart":false}),makeQuery(id+"F3.opExtrude","CAP_FACE",FACE,{"disambiguationData":[OSD([subQ3,subQ2,subQ1,subQ0]),ownerDisambiguation([makeQuery(id+"F2.imprint","IMPRINT",EDGE,{"derivedFrom":sQuery(id+"F2.wireOp",EDGE,"E21.MirrorCS")})])],"isStart":false}),makeQuery(id+"F3.opExtrude","CAP_FACE",FACE,{"disambiguationData":[OSD([subQ3,subQ2,subQ1,subQ0]),ownerDisambiguation([makeQuery(id+"F2.imprint","IMPRINT",EDGE,{"derivedFrom":sQuery(id+"F2.wireOp",EDGE,"E22.MirrorCS")})])],"isStart":false}),makeQuery(id+"F3.opExtrude","CAP_FACE",FACE,{"disambiguationData":[OSD([subQ3,subQ2,subQ1,subQ0]),ownerDisambiguation([makeQuery(id+"F2.imprint","IMPRINT",EDGE,{"derivedFrom":sQuery(id+"F2.wireOp",EDGE,"E42.MirrorCS")})])],"isStart":false}),makeQuery(id+"F3.opExtrude","CAP_FACE",FACE,{"disambiguationData":[OSD([subQ3,subQ2,subQ1,subQ0]),ownerDisambiguation([makeQuery(id+"F2.imprint","IMPRINT",EDGE,{"derivedFrom":sQuery(id+"F2.wireOp",EDGE,"E43.MirrorCS")})])],"isStart":false}),makeQuery(id+"F3.opExtrude","CAP_FACE",FACE,{"disambiguationData":[OSD([subQ3,subQ2,subQ1,subQ0]),ownerDisambiguation([makeQuery(id+"F2.imprint","IMPRINT",EDGE,{"derivedFrom":sQuery(id+"F2.wireOp",EDGE,"E49.MirrorCS")})])],"isStart":false}),makeQuery(id+"F3.opExtrude","CAP_FACE",FACE,{"disambiguationData":[OSD([subQ3,subQ2,subQ1,subQ0]),ownerDisambiguation([makeQuery(id+"F2.imprint","IMPRINT",EDGE,{"derivedFrom":sQuery(id+"F2.wireOp",EDGE,"E55.MirrorCS")})])],"isStart":false}),makeQuery(id+"F3.opExtrude","CAP_FACE",FACE,{"disambiguationData":[OSD([subQ3,subQ2,subQ1,subQ0]),ownerDisambiguation([makeQuery(id+"F2.imprint","IMPRINT",EDGE,{"derivedFrom":sQuery(id+"F2.wireOp",EDGE,"E57.MirrorCS")})])],"isStart":false}),makeQuery(id+"F3.opExtrude","CAP_FACE",FACE,{"disambiguationData":[OSD([subQ3,subQ2,subQ1,subQ0]),ownerDisambiguation([makeQuery(id+"F2.imprint","IMPRINT",EDGE,{"derivedFrom":sQuery(id+"F2.wireOp",EDGE,"E58.MirrorCS")})])],"isStart":false}),makeQuery(id+"F3.opExtrude","CAP_FACE",FACE,{"disambiguationData":[OSD([subQ3,subQ2,subQ1,subQ0]),ownerDisambiguation([makeQuery(id+"F2.imprint","IMPRINT",EDGE,{"derivedFrom":sQuery(id+"F2.wireOp",EDGE,"E59.MirrorCS")})])],"isStart":false}),makeQuery(id+"F3.opExtrude","CAP_FACE",FACE,{"disambiguationData":[OSD([subQ3,subQ2,subQ1,subQ0]),ownerDisambiguation([makeQuery(id+"F2.imprint","IMPRINT",EDGE,{"derivedFrom":sQuery(id+"F2.wireOp",EDGE,"E60.MirrorCS")})])],"isStart":false}),makeQuery(id+"F3.opExtrude","CAP_FACE",FACE,{"disambiguationData":[OSD([subQ3,subQ2,subQ1,subQ0]),ownerDisambiguation([makeQuery(id+"F2.imprint","IMPRINT",EDGE,{"derivedFrom":sQuery(id+"F2.wireOp",EDGE,"E63.MirrorCS")})])],"isStart":false}),makeQuery(id+"F3.opExtrude","CAP_FACE",FACE,{"disambiguationData":[OSD([subQ3,subQ2,subQ1,subQ0]),ownerDisambiguation([makeQuery(id+"F2.imprint","IMPRINT",EDGE,{"derivedFrom":sQuery(id+"F2.wireOp",EDGE,"E64.MirrorCS")})])],"isStart":false}),makeQuery(id+"F3.opExtrude","CAP_FACE",FACE,{"disambiguationData":[OSD([subQ3,subQ2,subQ1,subQ0]),ownerDisambiguation([makeQuery(id+"F2.imprint","IMPRINT",EDGE,{"derivedFrom":sQuery(id+"F2.wireOp",EDGE,"E65.MirrorCS")})])],"isStart":false}),makeQuery(id+"F3.opExtrude","CAP_FACE",FACE,{"disambiguationData":[OSD([subQ3,subQ2,subQ1,subQ0]),ownerDisambiguation([makeQuery(id+"F2.imprint","IMPRINT",EDGE,{"derivedFrom":sQuery(id+"F2.wireOp",EDGE,"E67.MirrorCS")})])],"isStart":false}),makeQuery(id+"F3.opExtrude","CAP_FACE",FACE,{"disambiguationData":[OSD([subQ3,subQ2,subQ1,subQ0]),ownerDisambiguation([makeQuery(id+"F2.imprint","IMPRINT",EDGE,{"derivedFrom":sQuery(id+"F2.wireOp",EDGE,"E71.MirrorCS")})])],"isStart":false}),makeQuery(id+"F3.opExtrude","CAP_FACE",FACE,{"disambiguationData":[OSD([subQ3,subQ2,subQ1,subQ0]),ownerDisambiguation([makeQuery(id+"F2.imprint","IMPRINT",EDGE,{"derivedFrom":sQuery(id+"F2.wireOp",EDGE,"E76.MirrorCS")})])],"isStart":false}),makeQuery(id+"F3.opExtrude","CAP_FACE",FACE,{"disambiguationData":[OSD([subQ3,subQ2,subQ1,subQ0]),ownerDisambiguation([makeQuery(id+"F2.imprint","IMPRINT",EDGE,{"derivedFrom":sQuery(id+"F2.wireOp",EDGE,"E82.MirrorCS")})])],"isStart":false}),makeQuery(id+"F3.opExtrude","CAP_FACE",FACE,{"disambiguationData":[OSD([subQ3,subQ2,subQ1,subQ0]),ownerDisambiguation([makeQuery(id+"F2.imprint","IMPRINT",EDGE,{"derivedFrom":sQuery(id+"F2.wireOp",EDGE,"E100.MirrorCS")})])],"isStart":false})]});}
            var sketch = newSketch(context, id + "F6", { "sketchPlane" : qUnion([Q0])});
            skLineSegment(sketch, "E122.bottom", {"start": v(-198, 12) * mm, "end": v(-186, 12) * mm});
            skLineSegment(sketch, "E122.top", {"start": v(-198, 19) * mm, "end": v(-186, 19) * mm});
            skLineSegment(sketch, "E122.left", {"start": v(-198, 12) * mm, "end": v(-198, 19) * mm});
            skLineSegment(sketch, "E122.right", {"start": v(-186, 12) * mm, "end": v(-186, 19) * mm});
            skLineSegment(sketch, "E123", {"start": v(-189, 0) * mm, "end": v(-172.05, 0) * mm, "construction": true});
            skPoint(sketch, "E123.endSnap0", {"position": v(-189, 0) * mm});
            skLineSegment(sketch, "E124.MirrorCS", {"start": v(-198, -12) * mm, "end": v(-198, -19) * mm});
            skLineSegment(sketch, "E125.MirrorCS", {"start": v(-186, -12) * mm, "end": v(-186, -19) * mm});
            skLineSegment(sketch, "E126.MirrorCS", {"start": v(-198, -19) * mm, "end": v(-186, -19) * mm});
            skLineSegment(sketch, "E127.MirrorCS", {"start": v(-198, -12) * mm, "end": v(-186, -12) * mm});
            skLineSegment(sketch, "E128", {"start": v(0, 0) * mm, "end": v(0, 7.32) * mm, "construction": true});
            skLineSegment(sketch, "E129.MirrorCS", {"start": v(186, -12) * mm, "end": v(186, -19) * mm});
            skLineSegment(sketch, "E130.MirrorCS", {"start": v(198, -12) * mm, "end": v(198, -19) * mm});
            skLineSegment(sketch, "E131.MirrorCS", {"start": v(186, 12) * mm, "end": v(186, 19) * mm});
            skLineSegment(sketch, "E132.MirrorCS", {"start": v(198, 12) * mm, "end": v(198, 19) * mm});
            skLineSegment(sketch, "E133.MirrorCS", {"start": v(198, -19) * mm, "end": v(186, -19) * mm});
            skLineSegment(sketch, "E134.MirrorCS", {"start": v(198, -12) * mm, "end": v(186, -12) * mm});
            skLineSegment(sketch, "E135.MirrorCS", {"start": v(189, 0) * mm, "end": v(172.05, 0) * mm, "construction": true});
            skLineSegment(sketch, "E136.MirrorCS", {"start": v(198, 19) * mm, "end": v(186, 19) * mm});
            skLineSegment(sketch, "E137.MirrorCS", {"start": v(198, 12) * mm, "end": v(186, 12) * mm});
            skPoint(sketch, "E138.MirrorP", {"position": v(189, 0) * mm});
            skSolve(sketch);
        }
        {
            var Q0;
            Q0=makeQuery(id+"F6.imprint","IMPRINT",FACE,{"disambiguationData":[TD([[makeQuery(id+"F6.imprint","IMPRINT",EDGE,{"derivedFrom":sQuery(id+"F6.wireOp",EDGE,"E131.MirrorCS")}),1.0]])]});
            var Q1;
            Q1=makeQuery(id+"F6.imprint","IMPRINT",FACE,{"disambiguationData":[TD([[makeQuery(id+"F6.imprint","IMPRINT",EDGE,{"derivedFrom":sQuery(id+"F6.wireOp",EDGE,"E129.MirrorCS")}),-1.0]])]});
            var Q2;
            Q2=makeQuery(id+"F6.imprint","IMPRINT",FACE,{"disambiguationData":[TD([[makeQuery(id+"F6.imprint","IMPRINT",EDGE,{"derivedFrom":sQuery(id+"F6.wireOp",EDGE,"E122.bottom")}),1.0]])]});
            var Q3;
            Q3=makeQuery(id+"F6.imprint","IMPRINT",FACE,{"disambiguationData":[TD([[makeQuery(id+"F6.imprint","IMPRINT",EDGE,{"derivedFrom":sQuery(id+"F6.wireOp",EDGE,"E124.MirrorCS")}),1.0]])]});
            var Q4;
            Q4 = qConstructionFilter(qBodyType(qCreatedBy(id + "F6" ,EDGE), BodyType.WIRE), ConstructionObject.NO);
            var Q5;
            Q5=makeQuery(id+"F3.boolean.opBoolean","MERGE",FACE,{"derivedFrom":[makeQuery(id+"F1.opExtrude","CAP_FACE",FACE,{"disambiguationData":[OSD([sQuery(id+"F0.wireOp",EDGE,"E0.bottom"),sQuery(id+"F0.wireOp",EDGE,"E0.top"),sQuery(id+"F0.wireOp",EDGE,"E0.left"),sQuery(id+"F0.wireOp",EDGE,"E0.right")])],"isStart":false}),makeQuery(id+"F3.opExtrude","CAP_FACE",FACE,{"disambiguationData":[OSD([sQuery(id+"F2.wireOp",EDGE,"E3.bottom"),sQuery(id+"F2.wireOp",EDGE,"E3.top"),sQuery(id+"F2.wireOp",EDGE,"E3.left"),sQuery(id+"F2.wireOp",EDGE,"E3.right")])],"isStart":true}),makeQuery(id+"F3.opExtrude","CAP_FACE",FACE,{"disambiguationData":[OSD([sQuery(id+"F2.wireOp",EDGE,"E5.1.0.0"),sQuery(id+"F2.wireOp",EDGE,"E5.1.0.1"),sQuery(id+"F2.wireOp",EDGE,"E5.1.0.2"),sQuery(id+"F2.wireOp",EDGE,"E5.1.0.3")])],"isStart":true}),makeQuery(id+"F3.opExtrude","CAP_FACE",FACE,{"disambiguationData":[OSD([sQuery(id+"F2.wireOp",EDGE,"E5.2.0.0"),sQuery(id+"F2.wireOp",EDGE,"E5.2.0.1"),sQuery(id+"F2.wireOp",EDGE,"E5.2.0.2"),sQuery(id+"F2.wireOp",EDGE,"E5.2.0.3")])],"isStart":true}),makeQuery(id+"F3.opExtrude","CAP_FACE",FACE,{"disambiguationData":[OSD([sQuery(id+"F2.wireOp",EDGE,"E5.3.0.0"),sQuery(id+"F2.wireOp",EDGE,"E5.3.0.1"),sQuery(id+"F2.wireOp",EDGE,"E5.3.0.2"),sQuery(id+"F2.wireOp",EDGE,"E5.3.0.3")])],"isStart":true}),makeQuery(id+"F3.opExtrude","CAP_FACE",FACE,{"disambiguationData":[OSD([sQuery(id+"F2.wireOp",EDGE,"E5.4.0.0"),sQuery(id+"F2.wireOp",EDGE,"E5.4.0.1"),sQuery(id+"F2.wireOp",EDGE,"E5.4.0.2"),sQuery(id+"F2.wireOp",EDGE,"E5.4.0.3")])],"isStart":true}),makeQuery(id+"F3.opExtrude","CAP_FACE",FACE,{"disambiguationData":[OSD([sQuery(id+"F2.wireOp",EDGE,"E5.5.0.0"),sQuery(id+"F2.wireOp",EDGE,"E5.5.0.1"),sQuery(id+"F2.wireOp",EDGE,"E5.5.0.2"),sQuery(id+"F2.wireOp",EDGE,"E5.5.0.3")])],"isStart":true}),makeQuery(id+"F3.opExtrude","CAP_FACE",FACE,{"disambiguationData":[OSD([sQuery(id+"F2.wireOp",EDGE,"E5.6.0.0"),sQuery(id+"F2.wireOp",EDGE,"E5.6.0.1"),sQuery(id+"F2.wireOp",EDGE,"E5.6.0.2"),sQuery(id+"F2.wireOp",EDGE,"E5.6.0.3")])],"isStart":true}),makeQuery(id+"F3.opExtrude","CAP_FACE",FACE,{"disambiguationData":[OSD([sQuery(id+"F2.wireOp",EDGE,"E5.7.0.0"),sQuery(id+"F2.wireOp",EDGE,"E5.7.0.1"),sQuery(id+"F2.wireOp",EDGE,"E5.7.0.2"),sQuery(id+"F2.wireOp",EDGE,"E5.7.0.3")])],"isStart":true}),makeQuery(id+"F3.opExtrude","CAP_FACE",FACE,{"disambiguationData":[OSD([sQuery(id+"F2.wireOp",EDGE,"E6.MirrorCS"),sQuery(id+"F2.wireOp",EDGE,"E8.MirrorCS"),sQuery(id+"F2.wireOp",EDGE,"E14.MirrorCS"),sQuery(id+"F2.wireOp",EDGE,"E18.MirrorCS")])],"isStart":true}),makeQuery(id+"F3.opExtrude","CAP_FACE",FACE,{"disambiguationData":[OSD([sQuery(id+"F2.wireOp",EDGE,"E11.MirrorCS"),sQuery(id+"F2.wireOp",EDGE,"E12.MirrorCS"),sQuery(id+"F2.wireOp",EDGE,"E25.MirrorCS"),sQuery(id+"F2.wireOp",EDGE,"E27.MirrorCS")])],"isStart":true}),makeQuery(id+"F3.opExtrude","CAP_FACE",FACE,{"disambiguationData":[OSD([sQuery(id+"F2.wireOp",EDGE,"E13.MirrorCS"),sQuery(id+"F2.wireOp",EDGE,"E28.MirrorCS"),sQuery(id+"F2.wireOp",EDGE,"E32.MirrorCS"),sQuery(id+"F2.wireOp",EDGE,"E38.MirrorCS")])],"isStart":true}),makeQuery(id+"F3.opExtrude","CAP_FACE",FACE,{"disambiguationData":[OSD([sQuery(id+"F2.wireOp",EDGE,"E15.MirrorCS"),sQuery(id+"F2.wireOp",EDGE,"E26.MirrorCS"),sQuery(id+"F2.wireOp",EDGE,"E34.MirrorCS"),sQuery(id+"F2.wireOp",EDGE,"E39.MirrorCS")])],"isStart":true}),makeQuery(id+"F3.opExtrude","CAP_FACE",FACE,{"disambiguationData":[OSD([sQuery(id+"F2.wireOp",EDGE,"E16.MirrorCS"),sQuery(id+"F2.wireOp",EDGE,"E17.MirrorCS"),sQuery(id+"F2.wireOp",EDGE,"E33.MirrorCS"),sQuery(id+"F2.wireOp",EDGE,"E35.MirrorCS")])],"isStart":true}),makeQuery(id+"F3.opExtrude","CAP_FACE",FACE,{"disambiguationData":[OSD([sQuery(id+"F2.wireOp",EDGE,"E19.MirrorCS"),sQuery(id+"F2.wireOp",EDGE,"E20.MirrorCS"),sQuery(id+"F2.wireOp",EDGE,"E23.MirrorCS"),sQuery(id+"F2.wireOp",EDGE,"E24.MirrorCS")])],"isStart":true}),makeQuery(id+"F3.opExtrude","CAP_FACE",FACE,{"disambiguationData":[OSD([sQuery(id+"F2.wireOp",EDGE,"E21.MirrorCS"),sQuery(id+"F2.wireOp",EDGE,"E30.MirrorCS"),sQuery(id+"F2.wireOp",EDGE,"E36.MirrorCS"),sQuery(id+"F2.wireOp",EDGE,"E37.MirrorCS")])],"isStart":true}),makeQuery(id+"F3.opExtrude","CAP_FACE",FACE,{"disambiguationData":[OSD([sQuery(id+"F2.wireOp",EDGE,"E22.MirrorCS"),sQuery(id+"F2.wireOp",EDGE,"E29.MirrorCS"),sQuery(id+"F2.wireOp",EDGE,"E31.MirrorCS"),sQuery(id+"F2.wireOp",EDGE,"E40.MirrorCS")])],"isStart":true}),makeQuery(id+"F3.opExtrude","CAP_FACE",FACE,{"disambiguationData":[OSD([sQuery(id+"F2.wireOp",EDGE,"E42.MirrorCS"),sQuery(id+"F2.wireOp",EDGE,"E45.MirrorCS"),sQuery(id+"F2.wireOp",EDGE,"E50.MirrorCS"),sQuery(id+"F2.wireOp",EDGE,"E83.MirrorCS")])],"isStart":true}),makeQuery(id+"F3.opExtrude","CAP_FACE",FACE,{"disambiguationData":[OSD([sQuery(id+"F2.wireOp",EDGE,"E43.MirrorCS"),sQuery(id+"F2.wireOp",EDGE,"E47.MirrorCS"),sQuery(id+"F2.wireOp",EDGE,"E48.MirrorCS"),sQuery(id+"F2.wireOp",EDGE,"E105.MirrorCS")])],"isStart":true}),makeQuery(id+"F3.opExtrude","CAP_FACE",FACE,{"disambiguationData":[OSD([sQuery(id+"F2.wireOp",EDGE,"E49.MirrorCS"),sQuery(id+"F2.wireOp",EDGE,"E54.MirrorCS"),sQuery(id+"F2.wireOp",EDGE,"E72.MirrorCS"),sQuery(id+"F2.wireOp",EDGE,"E96.MirrorCS")])],"isStart":true}),makeQuery(id+"F3.opExtrude","CAP_FACE",FACE,{"disambiguationData":[OSD([sQuery(id+"F2.wireOp",EDGE,"E55.MirrorCS"),sQuery(id+"F2.wireOp",EDGE,"E62.MirrorCS"),sQuery(id+"F2.wireOp",EDGE,"E80.MirrorCS"),sQuery(id+"F2.wireOp",EDGE,"E106.MirrorCS")])],"isStart":true}),makeQuery(id+"F3.opExtrude","CAP_FACE",FACE,{"disambiguationData":[OSD([sQuery(id+"F2.wireOp",EDGE,"E57.MirrorCS"),sQuery(id+"F2.wireOp",EDGE,"E68.MirrorCS"),sQuery(id+"F2.wireOp",EDGE,"E107.MirrorCS"),sQuery(id+"F2.wireOp",EDGE,"E108.MirrorCS")])],"isStart":true}),makeQuery(id+"F3.opExtrude","CAP_FACE",FACE,{"disambiguationData":[OSD([sQuery(id+"F2.wireOp",EDGE,"E58.MirrorCS"),sQuery(id+"F2.wireOp",EDGE,"E73.MirrorCS"),sQuery(id+"F2.wireOp",EDGE,"E91.MirrorCS"),sQuery(id+"F2.wireOp",EDGE,"E92.MirrorCS")])],"isStart":true}),makeQuery(id+"F3.opExtrude","CAP_FACE",FACE,{"disambiguationData":[OSD([sQuery(id+"F2.wireOp",EDGE,"E59.MirrorCS"),sQuery(id+"F2.wireOp",EDGE,"E61.MirrorCS"),sQuery(id+"F2.wireOp",EDGE,"E69.MirrorCS"),sQuery(id+"F2.wireOp",EDGE,"E70.MirrorCS")])],"isStart":true}),makeQuery(id+"F3.opExtrude","CAP_FACE",FACE,{"disambiguationData":[OSD([sQuery(id+"F2.wireOp",EDGE,"E60.MirrorCS"),sQuery(id+"F2.wireOp",EDGE,"E81.MirrorCS"),sQuery(id+"F2.wireOp",EDGE,"E87.MirrorCS"),sQuery(id+"F2.wireOp",EDGE,"E101.MirrorCS")])],"isStart":true}),makeQuery(id+"F3.opExtrude","CAP_FACE",FACE,{"disambiguationData":[OSD([sQuery(id+"F2.wireOp",EDGE,"E63.MirrorCS"),sQuery(id+"F2.wireOp",EDGE,"E78.MirrorCS"),sQuery(id+"F2.wireOp",EDGE,"E79.MirrorCS"),sQuery(id+"F2.wireOp",EDGE,"E90.MirrorCS")])],"isStart":true}),makeQuery(id+"F3.opExtrude","CAP_FACE",FACE,{"disambiguationData":[OSD([sQuery(id+"F2.wireOp",EDGE,"E64.MirrorCS"),sQuery(id+"F2.wireOp",EDGE,"E85.MirrorCS"),sQuery(id+"F2.wireOp",EDGE,"E86.MirrorCS"),sQuery(id+"F2.wireOp",EDGE,"E103.MirrorCS")])],"isStart":true}),makeQuery(id+"F3.opExtrude","CAP_FACE",FACE,{"disambiguationData":[OSD([sQuery(id+"F2.wireOp",EDGE,"E65.MirrorCS"),sQuery(id+"F2.wireOp",EDGE,"E66.MirrorCS"),sQuery(id+"F2.wireOp",EDGE,"E89.MirrorCS"),sQuery(id+"F2.wireOp",EDGE,"E93.MirrorCS")])],"isStart":true}),makeQuery(id+"F3.opExtrude","CAP_FACE",FACE,{"disambiguationData":[OSD([sQuery(id+"F2.wireOp",EDGE,"E67.MirrorCS"),sQuery(id+"F2.wireOp",EDGE,"E74.MirrorCS"),sQuery(id+"F2.wireOp",EDGE,"E75.MirrorCS"),sQuery(id+"F2.wireOp",EDGE,"E77.MirrorCS")])],"isStart":true}),makeQuery(id+"F3.opExtrude","CAP_FACE",FACE,{"disambiguationData":[OSD([sQuery(id+"F2.wireOp",EDGE,"E71.MirrorCS"),sQuery(id+"F2.wireOp",EDGE,"E88.MirrorCS"),sQuery(id+"F2.wireOp",EDGE,"E98.MirrorCS"),sQuery(id+"F2.wireOp",EDGE,"E111.MirrorCS")])],"isStart":true}),makeQuery(id+"F3.opExtrude","CAP_FACE",FACE,{"disambiguationData":[OSD([sQuery(id+"F2.wireOp",EDGE,"E76.MirrorCS"),sQuery(id+"F2.wireOp",EDGE,"E94.MirrorCS"),sQuery(id+"F2.wireOp",EDGE,"E99.MirrorCS"),sQuery(id+"F2.wireOp",EDGE,"E104.MirrorCS")])],"isStart":true}),makeQuery(id+"F3.opExtrude","CAP_FACE",FACE,{"disambiguationData":[OSD([sQuery(id+"F2.wireOp",EDGE,"E82.MirrorCS"),sQuery(id+"F2.wireOp",EDGE,"E84.MirrorCS"),sQuery(id+"F2.wireOp",EDGE,"E95.MirrorCS"),sQuery(id+"F2.wireOp",EDGE,"E97.MirrorCS")])],"isStart":true}),makeQuery(id+"F3.opExtrude","CAP_FACE",FACE,{"disambiguationData":[OSD([sQuery(id+"F2.wireOp",EDGE,"E100.MirrorCS"),sQuery(id+"F2.wireOp",EDGE,"E102.MirrorCS"),sQuery(id+"F2.wireOp",EDGE,"E109.MirrorCS"),sQuery(id+"F2.wireOp",EDGE,"E110.MirrorCS")])],"isStart":true})]});
            extrude(context, id + "F7", {"entities" : qUnion([Q0, Q1, Q2, Q3]), "operationType" : NewBodyOperationType.ADD, "surfaceEntities" : qUnion([Q4]), "endBound" : BoundingType.UP_TO_SURFACE, "oppositeDirection" : true, "endBoundEntityFace" : qUnion([Q5]), "depth" : 12 * mm});
        }
        {
            var Q0;
            {var subQ0=sQuery(id+"F0.wireOp",EDGE,"E0.right");var subQ1=sQuery(id+"F0.wireOp",EDGE,"E0.left");var subQ2=sQuery(id+"F0.wireOp",EDGE,"E0.top");var subQ3=sQuery(id+"F0.wireOp",EDGE,"E0.bottom");Q0=makeQuery(id+"F7.boolean.opBoolean","MERGE",FACE,{"derivedFrom":[makeQuery(id+"F3.boolean.opBoolean","MERGE",FACE,{"derivedFrom":[makeQuery(id+"F1.opExtrude","CAP_FACE",FACE,{"disambiguationData":[OSD([subQ3,subQ2,subQ1,subQ0])],"isStart":true}),makeQuery(id+"F3.opExtrude","CAP_FACE",FACE,{"disambiguationData":[OSD([subQ3,subQ2,subQ1,subQ0]),ownerDisambiguation([makeQuery(id+"F2.imprint","IMPRINT",EDGE,{"derivedFrom":sQuery(id+"F2.wireOp",EDGE,"E3.bottom")})])],"isStart":false}),makeQuery(id+"F3.opExtrude","CAP_FACE",FACE,{"disambiguationData":[OSD([subQ3,subQ2,subQ1,subQ0]),ownerDisambiguation([makeQuery(id+"F2.imprint","IMPRINT",EDGE,{"derivedFrom":sQuery(id+"F2.wireOp",EDGE,"E5.1.0.0")})])],"isStart":false}),makeQuery(id+"F3.opExtrude","CAP_FACE",FACE,{"disambiguationData":[OSD([subQ3,subQ2,subQ1,subQ0]),ownerDisambiguation([makeQuery(id+"F2.imprint","IMPRINT",EDGE,{"derivedFrom":sQuery(id+"F2.wireOp",EDGE,"E5.2.0.0")})])],"isStart":false}),makeQuery(id+"F3.opExtrude","CAP_FACE",FACE,{"disambiguationData":[OSD([subQ3,subQ2,subQ1,subQ0]),ownerDisambiguation([makeQuery(id+"F2.imprint","IMPRINT",EDGE,{"derivedFrom":sQuery(id+"F2.wireOp",EDGE,"E5.3.0.0")})])],"isStart":false}),makeQuery(id+"F3.opExtrude","CAP_FACE",FACE,{"disambiguationData":[OSD([subQ3,subQ2,subQ1,subQ0]),ownerDisambiguation([makeQuery(id+"F2.imprint","IMPRINT",EDGE,{"derivedFrom":sQuery(id+"F2.wireOp",EDGE,"E5.4.0.0")})])],"isStart":false}),makeQuery(id+"F3.opExtrude","CAP_FACE",FACE,{"disambiguationData":[OSD([subQ3,subQ2,subQ1,subQ0]),ownerDisambiguation([makeQuery(id+"F2.imprint","IMPRINT",EDGE,{"derivedFrom":sQuery(id+"F2.wireOp",EDGE,"E5.5.0.0")})])],"isStart":false}),makeQuery(id+"F3.opExtrude","CAP_FACE",FACE,{"disambiguationData":[OSD([subQ3,subQ2,subQ1,subQ0]),ownerDisambiguation([makeQuery(id+"F2.imprint","IMPRINT",EDGE,{"derivedFrom":sQuery(id+"F2.wireOp",EDGE,"E5.6.0.0")})])],"isStart":false}),makeQuery(id+"F3.opExtrude","CAP_FACE",FACE,{"disambiguationData":[OSD([subQ3,subQ2,subQ1,subQ0]),ownerDisambiguation([makeQuery(id+"F2.imprint","IMPRINT",EDGE,{"derivedFrom":sQuery(id+"F2.wireOp",EDGE,"E5.7.0.0")})])],"isStart":false}),makeQuery(id+"F3.opExtrude","CAP_FACE",FACE,{"disambiguationData":[OSD([subQ3,subQ2,subQ1,subQ0]),ownerDisambiguation([makeQuery(id+"F2.imprint","IMPRINT",EDGE,{"derivedFrom":sQuery(id+"F2.wireOp",EDGE,"E6.MirrorCS")})])],"isStart":false}),makeQuery(id+"F3.opExtrude","CAP_FACE",FACE,{"disambiguationData":[OSD([subQ3,subQ2,subQ1,subQ0]),ownerDisambiguation([makeQuery(id+"F2.imprint","IMPRINT",EDGE,{"derivedFrom":sQuery(id+"F2.wireOp",EDGE,"E11.MirrorCS")})])],"isStart":false}),makeQuery(id+"F3.opExtrude","CAP_FACE",FACE,{"disambiguationData":[OSD([subQ3,subQ2,subQ1,subQ0]),ownerDisambiguation([makeQuery(id+"F2.imprint","IMPRINT",EDGE,{"derivedFrom":sQuery(id+"F2.wireOp",EDGE,"E13.MirrorCS")})])],"isStart":false}),makeQuery(id+"F3.opExtrude","CAP_FACE",FACE,{"disambiguationData":[OSD([subQ3,subQ2,subQ1,subQ0]),ownerDisambiguation([makeQuery(id+"F2.imprint","IMPRINT",EDGE,{"derivedFrom":sQuery(id+"F2.wireOp",EDGE,"E15.MirrorCS")})])],"isStart":false}),makeQuery(id+"F3.opExtrude","CAP_FACE",FACE,{"disambiguationData":[OSD([subQ3,subQ2,subQ1,subQ0]),ownerDisambiguation([makeQuery(id+"F2.imprint","IMPRINT",EDGE,{"derivedFrom":sQuery(id+"F2.wireOp",EDGE,"E16.MirrorCS")})])],"isStart":false}),makeQuery(id+"F3.opExtrude","CAP_FACE",FACE,{"disambiguationData":[OSD([subQ3,subQ2,subQ1,subQ0]),ownerDisambiguation([makeQuery(id+"F2.imprint","IMPRINT",EDGE,{"derivedFrom":sQuery(id+"F2.wireOp",EDGE,"E19.MirrorCS")})])],"isStart":false}),makeQuery(id+"F3.opExtrude","CAP_FACE",FACE,{"disambiguationData":[OSD([subQ3,subQ2,subQ1,subQ0]),ownerDisambiguation([makeQuery(id+"F2.imprint","IMPRINT",EDGE,{"derivedFrom":sQuery(id+"F2.wireOp",EDGE,"E21.MirrorCS")})])],"isStart":false}),makeQuery(id+"F3.opExtrude","CAP_FACE",FACE,{"disambiguationData":[OSD([subQ3,subQ2,subQ1,subQ0]),ownerDisambiguation([makeQuery(id+"F2.imprint","IMPRINT",EDGE,{"derivedFrom":sQuery(id+"F2.wireOp",EDGE,"E22.MirrorCS")})])],"isStart":false}),makeQuery(id+"F3.opExtrude","CAP_FACE",FACE,{"disambiguationData":[OSD([subQ3,subQ2,subQ1,subQ0]),ownerDisambiguation([makeQuery(id+"F2.imprint","IMPRINT",EDGE,{"derivedFrom":sQuery(id+"F2.wireOp",EDGE,"E42.MirrorCS")})])],"isStart":false}),makeQuery(id+"F3.opExtrude","CAP_FACE",FACE,{"disambiguationData":[OSD([subQ3,subQ2,subQ1,subQ0]),ownerDisambiguation([makeQuery(id+"F2.imprint","IMPRINT",EDGE,{"derivedFrom":sQuery(id+"F2.wireOp",EDGE,"E43.MirrorCS")})])],"isStart":false}),makeQuery(id+"F3.opExtrude","CAP_FACE",FACE,{"disambiguationData":[OSD([subQ3,subQ2,subQ1,subQ0]),ownerDisambiguation([makeQuery(id+"F2.imprint","IMPRINT",EDGE,{"derivedFrom":sQuery(id+"F2.wireOp",EDGE,"E49.MirrorCS")})])],"isStart":false}),makeQuery(id+"F3.opExtrude","CAP_FACE",FACE,{"disambiguationData":[OSD([subQ3,subQ2,subQ1,subQ0]),ownerDisambiguation([makeQuery(id+"F2.imprint","IMPRINT",EDGE,{"derivedFrom":sQuery(id+"F2.wireOp",EDGE,"E55.MirrorCS")})])],"isStart":false}),makeQuery(id+"F3.opExtrude","CAP_FACE",FACE,{"disambiguationData":[OSD([subQ3,subQ2,subQ1,subQ0]),ownerDisambiguation([makeQuery(id+"F2.imprint","IMPRINT",EDGE,{"derivedFrom":sQuery(id+"F2.wireOp",EDGE,"E57.MirrorCS")})])],"isStart":false}),makeQuery(id+"F3.opExtrude","CAP_FACE",FACE,{"disambiguationData":[OSD([subQ3,subQ2,subQ1,subQ0]),ownerDisambiguation([makeQuery(id+"F2.imprint","IMPRINT",EDGE,{"derivedFrom":sQuery(id+"F2.wireOp",EDGE,"E58.MirrorCS")})])],"isStart":false}),makeQuery(id+"F3.opExtrude","CAP_FACE",FACE,{"disambiguationData":[OSD([subQ3,subQ2,subQ1,subQ0]),ownerDisambiguation([makeQuery(id+"F2.imprint","IMPRINT",EDGE,{"derivedFrom":sQuery(id+"F2.wireOp",EDGE,"E59.MirrorCS")})])],"isStart":false}),makeQuery(id+"F3.opExtrude","CAP_FACE",FACE,{"disambiguationData":[OSD([subQ3,subQ2,subQ1,subQ0]),ownerDisambiguation([makeQuery(id+"F2.imprint","IMPRINT",EDGE,{"derivedFrom":sQuery(id+"F2.wireOp",EDGE,"E60.MirrorCS")})])],"isStart":false}),makeQuery(id+"F3.opExtrude","CAP_FACE",FACE,{"disambiguationData":[OSD([subQ3,subQ2,subQ1,subQ0]),ownerDisambiguation([makeQuery(id+"F2.imprint","IMPRINT",EDGE,{"derivedFrom":sQuery(id+"F2.wireOp",EDGE,"E63.MirrorCS")})])],"isStart":false}),makeQuery(id+"F3.opExtrude","CAP_FACE",FACE,{"disambiguationData":[OSD([subQ3,subQ2,subQ1,subQ0]),ownerDisambiguation([makeQuery(id+"F2.imprint","IMPRINT",EDGE,{"derivedFrom":sQuery(id+"F2.wireOp",EDGE,"E64.MirrorCS")})])],"isStart":false}),makeQuery(id+"F3.opExtrude","CAP_FACE",FACE,{"disambiguationData":[OSD([subQ3,subQ2,subQ1,subQ0]),ownerDisambiguation([makeQuery(id+"F2.imprint","IMPRINT",EDGE,{"derivedFrom":sQuery(id+"F2.wireOp",EDGE,"E65.MirrorCS")})])],"isStart":false}),makeQuery(id+"F3.opExtrude","CAP_FACE",FACE,{"disambiguationData":[OSD([subQ3,subQ2,subQ1,subQ0]),ownerDisambiguation([makeQuery(id+"F2.imprint","IMPRINT",EDGE,{"derivedFrom":sQuery(id+"F2.wireOp",EDGE,"E67.MirrorCS")})])],"isStart":false}),makeQuery(id+"F3.opExtrude","CAP_FACE",FACE,{"disambiguationData":[OSD([subQ3,subQ2,subQ1,subQ0]),ownerDisambiguation([makeQuery(id+"F2.imprint","IMPRINT",EDGE,{"derivedFrom":sQuery(id+"F2.wireOp",EDGE,"E71.MirrorCS")})])],"isStart":false}),makeQuery(id+"F3.opExtrude","CAP_FACE",FACE,{"disambiguationData":[OSD([subQ3,subQ2,subQ1,subQ0]),ownerDisambiguation([makeQuery(id+"F2.imprint","IMPRINT",EDGE,{"derivedFrom":sQuery(id+"F2.wireOp",EDGE,"E76.MirrorCS")})])],"isStart":false}),makeQuery(id+"F3.opExtrude","CAP_FACE",FACE,{"disambiguationData":[OSD([subQ3,subQ2,subQ1,subQ0]),ownerDisambiguation([makeQuery(id+"F2.imprint","IMPRINT",EDGE,{"derivedFrom":sQuery(id+"F2.wireOp",EDGE,"E82.MirrorCS")})])],"isStart":false}),makeQuery(id+"F3.opExtrude","CAP_FACE",FACE,{"disambiguationData":[OSD([subQ3,subQ2,subQ1,subQ0]),ownerDisambiguation([makeQuery(id+"F2.imprint","IMPRINT",EDGE,{"derivedFrom":sQuery(id+"F2.wireOp",EDGE,"E100.MirrorCS")})])],"isStart":false})]}),makeQuery(id+"F7.opExtrude","CAP_FACE",FACE,{"disambiguationData":[OSD([sQuery(id+"F6.wireOp",EDGE,"E122.bottom"),sQuery(id+"F6.wireOp",EDGE,"E122.top"),sQuery(id+"F6.wireOp",EDGE,"E122.left"),sQuery(id+"F6.wireOp",EDGE,"E122.right")])],"isStart":true}),makeQuery(id+"F7.opExtrude","CAP_FACE",FACE,{"disambiguationData":[OSD([sQuery(id+"F6.wireOp",EDGE,"E124.MirrorCS"),sQuery(id+"F6.wireOp",EDGE,"E125.MirrorCS"),sQuery(id+"F6.wireOp",EDGE,"E126.MirrorCS"),sQuery(id+"F6.wireOp",EDGE,"E127.MirrorCS")])],"isStart":true}),makeQuery(id+"F7.opExtrude","CAP_FACE",FACE,{"disambiguationData":[OSD([sQuery(id+"F6.wireOp",EDGE,"E129.MirrorCS"),sQuery(id+"F6.wireOp",EDGE,"E130.MirrorCS"),sQuery(id+"F6.wireOp",EDGE,"E133.MirrorCS"),sQuery(id+"F6.wireOp",EDGE,"E134.MirrorCS")])],"isStart":true}),makeQuery(id+"F7.opExtrude","CAP_FACE",FACE,{"disambiguationData":[OSD([sQuery(id+"F6.wireOp",EDGE,"E131.MirrorCS"),sQuery(id+"F6.wireOp",EDGE,"E132.MirrorCS"),sQuery(id+"F6.wireOp",EDGE,"E136.MirrorCS"),sQuery(id+"F6.wireOp",EDGE,"E137.MirrorCS")])],"isStart":true})]});}
            var sketch = newSketch(context, id + "F8", { "sketchPlane" : qUnion([Q0])});
            skLineSegment(sketch, "E139.bottom", {"start": v(189, 6) * mm, "end": v(186, 6) * mm});
            skLineSegment(sketch, "E139.top", {"start": v(189, -6) * mm, "end": v(186, -6) * mm});
            skLineSegment(sketch, "E139.left", {"start": v(189, 6) * mm, "end": v(189, -6) * mm});
            skLineSegment(sketch, "E139.right", {"start": v(186, 6) * mm, "end": v(186, -6) * mm});
            skLineSegment(sketch, "E140.bottom", {"start": v(-189, 6) * mm, "end": v(-186, 6) * mm});
            skLineSegment(sketch, "E140.top", {"start": v(-189, -6) * mm, "end": v(-186, -6) * mm});
            skLineSegment(sketch, "E140.left", {"start": v(-189, 6) * mm, "end": v(-189, -6) * mm});
            skLineSegment(sketch, "E140.right", {"start": v(-186, 6) * mm, "end": v(-186, -6) * mm});
            skLineSegment(sketch, "E141.bottom", {"start": v(-198, 19) * mm, "end": v(-195, 19) * mm});
            skLineSegment(sketch, "E141.top", {"start": v(-198, -19) * mm, "end": v(-195, -19) * mm});
            skLineSegment(sketch, "E141.left", {"start": v(-198, 19) * mm, "end": v(-198, -19) * mm});
            skLineSegment(sketch, "E141.right", {"start": v(-195, 19) * mm, "end": v(-195, -19) * mm});
            skLineSegment(sketch, "E142.bottom", {"start": v(198, 19) * mm, "end": v(195, 19) * mm});
            skLineSegment(sketch, "E142.top", {"start": v(198, -19) * mm, "end": v(195, -19) * mm});
            skLineSegment(sketch, "E142.left", {"start": v(198, 19) * mm, "end": v(198, -19) * mm});
            skLineSegment(sketch, "E142.right", {"start": v(195, 19) * mm, "end": v(195, -19) * mm});
            skSolve(sketch);
        }
        {
            var Q0;
            Q0 = qSketchRegion(id + "F8", true);
            extrude(context, id + "F9", {"entities" : qUnion([Q0]), "operationType" : NewBodyOperationType.REMOVE, "oppositeDirection" : true, "depth" : 25 * mm});
        }
    });
